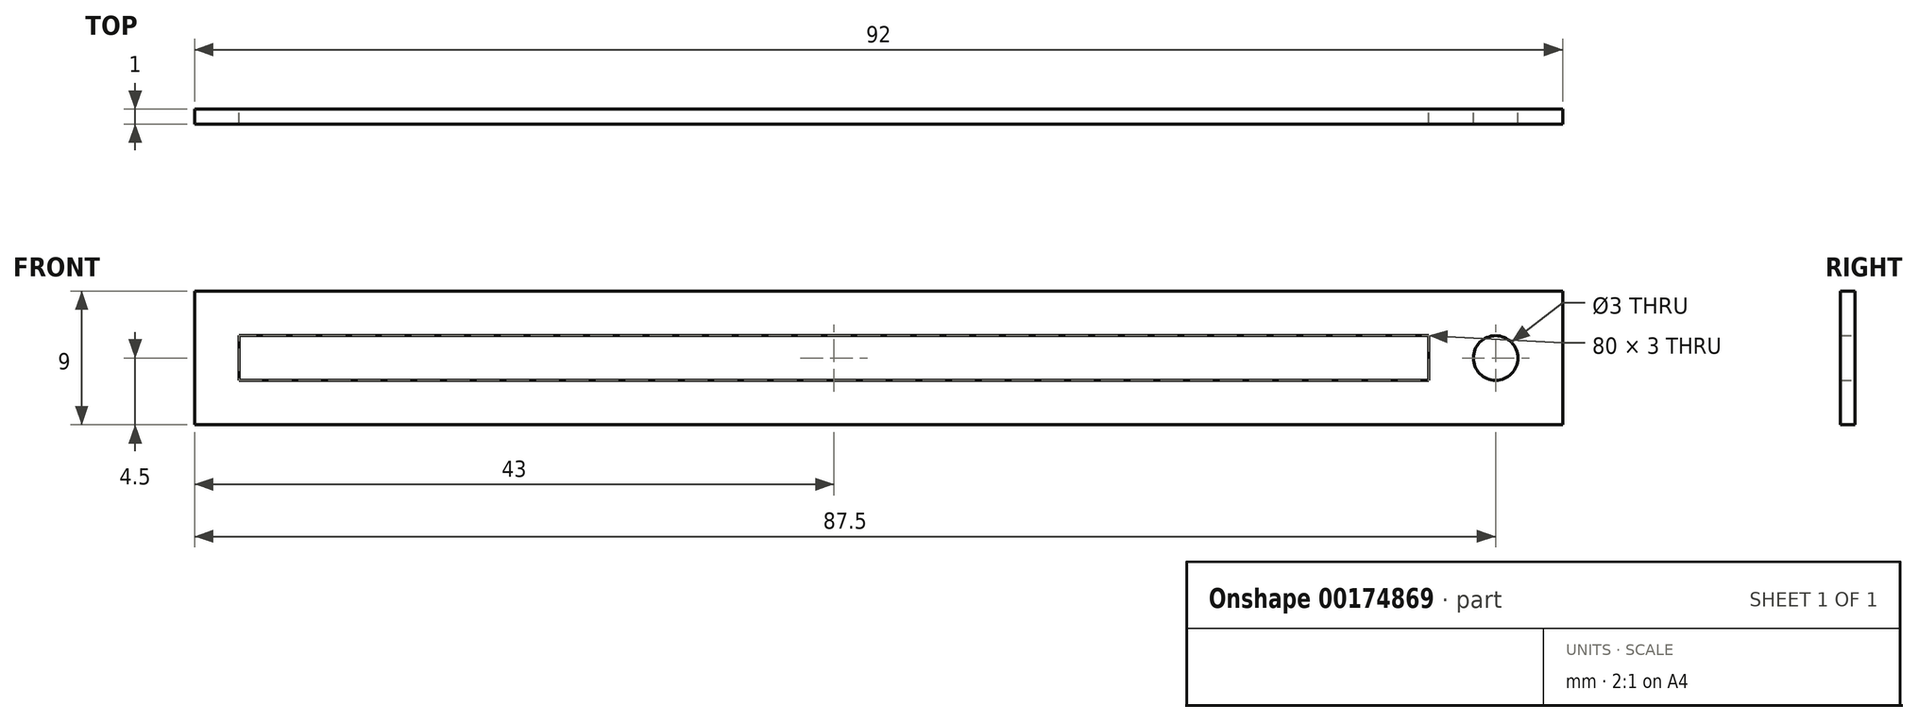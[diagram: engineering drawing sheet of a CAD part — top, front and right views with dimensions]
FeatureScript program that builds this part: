
annotation { "Feature Type Name" : "Feature", "Feature Type Description" : "" }
export const myFeature = defineFeature(function(context is Context, id is Id, definition is map)
    precondition{}
    {
        {
            var Q0;
            Q0=qCreatedBy(makeId("Front.planeOp"),FACE);
            var sketch = newSketch(context, id + "F0", { "sketchPlane" : qUnion([Q0])});
            skLineSegment(sketch, "E0.bottom", {"start": v(46, -4.5) * mm, "end": v(-46, -4.5) * mm});
            skLineSegment(sketch, "E0.top", {"start": v(46, 4.5) * mm, "end": v(-46, 4.5) * mm});
            skLineSegment(sketch, "E0.left", {"start": v(46, -4.5) * mm, "end": v(46, 4.5) * mm});
            skLineSegment(sketch, "E0.right", {"start": v(-46, -4.5) * mm, "end": v(-46, 4.5) * mm});
            skPoint(sketch, "E0.middle", {"position": v(0, 0) * mm});
            skLineSegment(sketch, "E1.bottom", {"start": v(-43, 1.5) * mm, "end": v(37, 1.5) * mm});
            skLineSegment(sketch, "E1.top", {"start": v(-43, -1.5) * mm, "end": v(37, -1.5) * mm});
            skLineSegment(sketch, "E1.left", {"start": v(-43, 1.5) * mm, "end": v(-43, -1.5) * mm});
            skLineSegment(sketch, "E1.right", {"start": v(37, 1.5) * mm, "end": v(37, -1.5) * mm});
            skCircle(sketch, "E2", {"center": v(41.5, 0) * mm, "radius": 1.5 * mm});
            skSolve(sketch);
        }
        {
            var Q0;
            Q0 = qSketchRegion(id + "F0", true);
            extrude(context, id + "F1", {"entities" : qUnion([Q0]), "depth" : 1 * mm});
        }
    });
